# Revit family: Benchmark-Laminate Top
name_source: partatom
category: Furniture
revit_build: Autodesk Revit 2016 (Build: 20150220_1215(x64)
units: mm (PartAtom-declared; Revit-internal decimal feet)

## family parameters
Always vertical = Yes
Cut with Voids When Loaded = No
OmniClass Number = 23.40.20.00
OmniClass Title = General Furniture and Specialties
Room Calculation Point = No
Shared = No
Work Plane-Based = No

## types (10) — shared parameters
Counter Finish = Solid Surface Countertop
Height(Cushion)Bottom = 0' - 9 1/2"
height(Laminate) = 1' - 3 1/2"

## per-type parameters (varying)
| type | Length | Width |
| 48x72 | 6' - 0" | 4' - 0" |
| 48x60 | 5' - 0" | 4' - 0" |
| 42x72 | 6' - 0" | 3' - 6" |
| 42x60 | 5' - 0" | 3' - 6" |
| 36x72 | 6' - 0" | 3' - 0" |
| 36x60 | 5' - 0" | 3' - 0" |
| 30x72 | 6' - 0" | 2' - 6" |
| 30x60 | 5' - 0" | 2' - 6" |
| 24x72 | 6' - 0" | 2' - 0" |
| 24x60 | 5' - 0" | 2' - 0" |

## geometry (parser evidence)
native form markers: Blend x2, Sweep x8
no freeform markers — native parametric forms only
